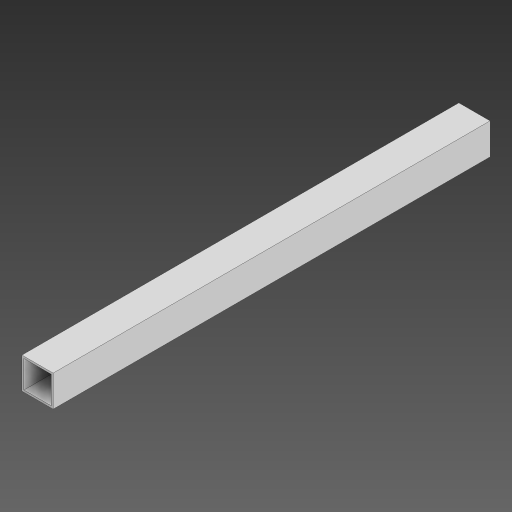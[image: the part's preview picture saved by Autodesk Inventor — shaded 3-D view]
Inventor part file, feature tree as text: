
AUTODESK INVENTOR PART (.ipt)
format: ipt  version: 2024 (Build 280153000, 153)  size: 88,576 bytes
history: native  units: in
note: dims shown in document units (in); Inventor stores cm internally (conversion verified against a paired STEP export)
features: extrude x1, sketch x1
ambient origin geometry x8: Origin, YZ Plane, XZ Plane, XY Plane, X Axis, Y Axis, Z Axis, Center Point
bodies: Solid1 (feature_tree)
feature tree (2):
  extrude  "Extrusion1"  Depth=1.0in
  sketch  "Sketch1"  dims[d0=1.0in d1=1.0in d2=0.0625in d3=14.0in d4=0.0in]
